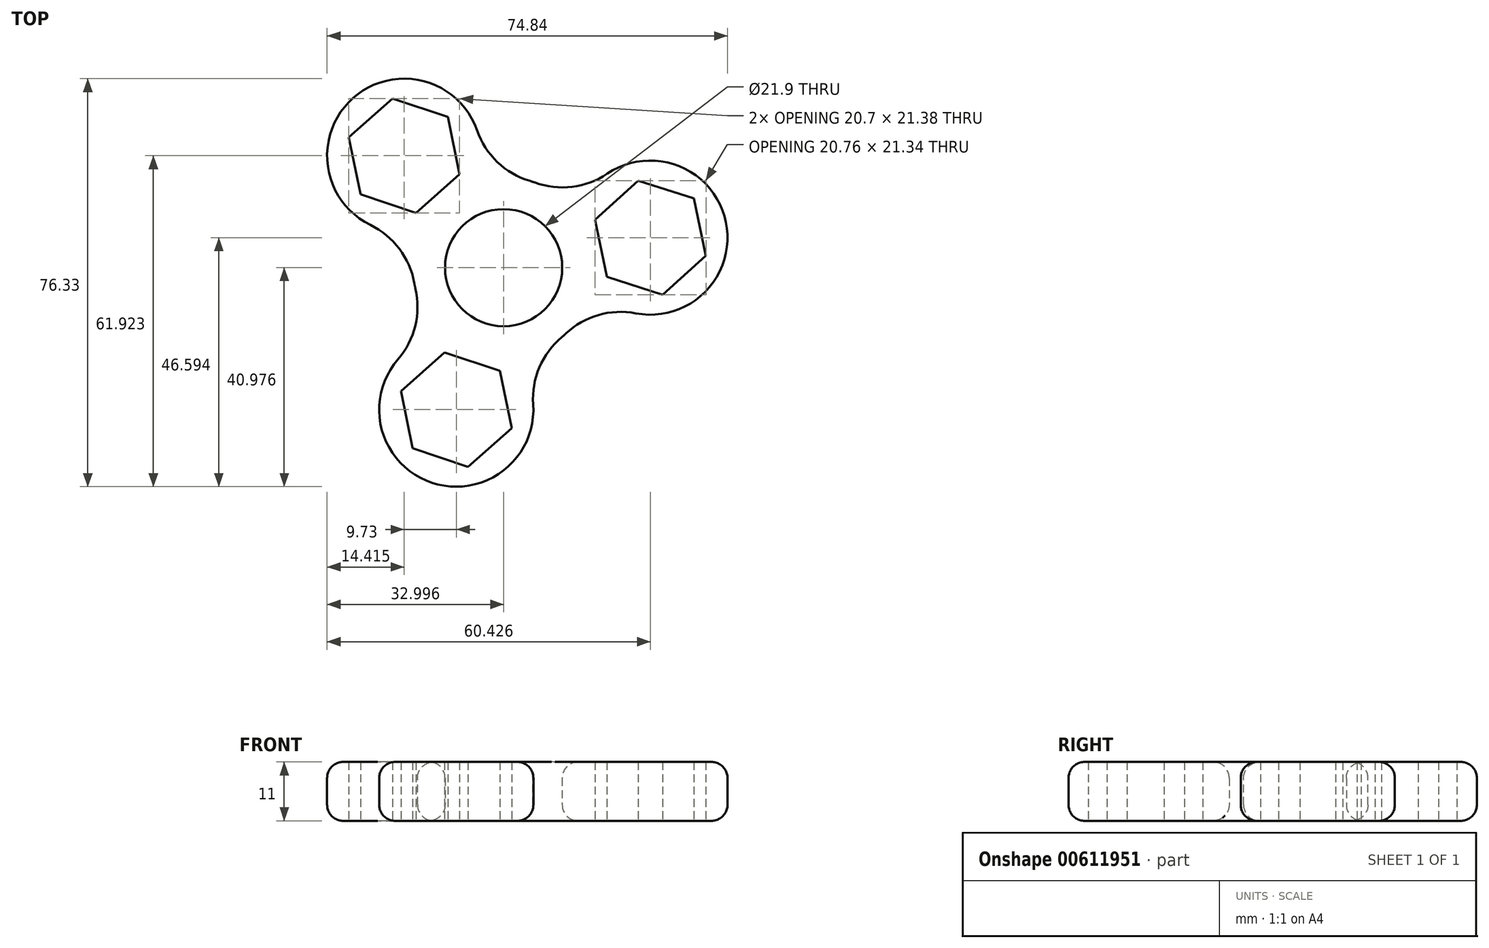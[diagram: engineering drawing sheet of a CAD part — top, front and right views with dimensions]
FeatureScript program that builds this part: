
annotation { "Feature Type Name" : "Feature", "Feature Type Description" : "" }
export const myFeature = defineFeature(function(context is Context, id is Id, definition is map)
    precondition{}
    {
        {
            var Q0;
            Q0=qCreatedBy(makeId("Top.planeOp"),FACE);
            var sketch = newSketch(context, id + "F0", { "sketchPlane" : qUnion([Q0])});
            skCircle(sketch, "E0", {"center": v(0.14, -0.37) * mm, "radius": 10.95 * mm});
            skCircle(sketch, "E1.0", {"center": v(0.14, -0.37) * mm, "radius": 16.95 * mm});
            skCircle(sketch, "E2.cCircle", {"center": v(0.14, -0.37) * mm, "radius": 14 * mm, "construction": true});
            skLineSegment(sketch, "E2.0", {"start": v(-18.44, 20.57) * mm, "end": v(27.57, 5.24) * mm, "construction": true});
            skLineSegment(sketch, "E2.1", {"start": v(27.57, 5.24) * mm, "end": v(-8.71, -26.94) * mm, "construction": true});
            skLineSegment(sketch, "E2.2", {"start": v(-8.71, -26.94) * mm, "end": v(-18.44, 20.57) * mm, "construction": true});
            skPoint(sketch, "E2.0.midPoint", {"position": v(4.56, 12.9) * mm});
            skCircle(sketch, "E3.cCircle", {"center": v(-18.44, 20.57) * mm, "radius": 9.45 * mm, "construction": true});
            skLineSegment(sketch, "E3.0", {"start": v(-28.8, 24.03) * mm, "end": v(-20.63, 31.26) * mm});
            skLineSegment(sketch, "E3.1", {"start": v(-20.63, 31.26) * mm, "end": v(-10.28, 27.8) * mm});
            skLineSegment(sketch, "E3.2", {"start": v(-10.28, 27.8) * mm, "end": v(-8.1, 17.12) * mm});
            skLineSegment(sketch, "E3.3", {"start": v(-8.1, 17.12) * mm, "end": v(-16.26, 9.88) * mm});
            skLineSegment(sketch, "E3.4", {"start": v(-16.26, 9.88) * mm, "end": v(-26.61, 13.34) * mm});
            skLineSegment(sketch, "E3.5", {"start": v(-26.61, 13.34) * mm, "end": v(-28.8, 24.03) * mm});
            skPoint(sketch, "E3.0.midPoint", {"position": v(-24.71, 27.65) * mm});
            skCircle(sketch, "E4.cCircle", {"center": v(27.57, 5.24) * mm, "radius": 9.45 * mm, "construction": true});
            skLineSegment(sketch, "E4.0", {"start": v(35.67, 12.55) * mm, "end": v(37.95, 1.88) * mm});
            skLineSegment(sketch, "E4.1", {"start": v(37.95, 1.88) * mm, "end": v(29.85, -5.43) * mm});
            skLineSegment(sketch, "E4.2", {"start": v(29.85, -5.43) * mm, "end": v(19.47, -2.07) * mm});
            skLineSegment(sketch, "E4.3", {"start": v(19.47, -2.07) * mm, "end": v(17.18, 8.6) * mm});
            skLineSegment(sketch, "E4.4", {"start": v(17.18, 8.6) * mm, "end": v(25.29, 15.91) * mm});
            skLineSegment(sketch, "E4.5", {"start": v(25.29, 15.91) * mm, "end": v(35.67, 12.55) * mm});
            skPoint(sketch, "E4.0.midPoint", {"position": v(36.8, 7.22) * mm});
            skCircle(sketch, "E5.cCircle", {"center": v(-8.71, -26.94) * mm, "radius": 9.45 * mm, "construction": true});
            skLineSegment(sketch, "E5.0", {"start": v(-6.53, -37.63) * mm, "end": v(-16.88, -34.17) * mm});
            skLineSegment(sketch, "E5.1", {"start": v(-16.88, -34.17) * mm, "end": v(-19.06, -23.48) * mm});
            skLineSegment(sketch, "E5.2", {"start": v(-19.06, -23.48) * mm, "end": v(-10.9, -16.25) * mm});
            skLineSegment(sketch, "E5.3", {"start": v(-10.9, -16.25) * mm, "end": v(-0.55, -19.7) * mm});
            skLineSegment(sketch, "E5.4", {"start": v(-0.55, -19.7) * mm, "end": v(1.63, -30.4) * mm});
            skLineSegment(sketch, "E5.5", {"start": v(1.63, -30.4) * mm, "end": v(-6.53, -37.63) * mm});
            skPoint(sketch, "E5.0.midPoint", {"position": v(-11.7, -35.9) * mm});
            skCircle(sketch, "E6", {"center": v(-8.71, -26.94) * mm, "radius": 14.41 * mm});
            skCircle(sketch, "E7", {"center": v(27.57, 5.24) * mm, "radius": 14.41 * mm});
            skCircle(sketch, "E8", {"center": v(-18.44, 20.57) * mm, "radius": 14.41 * mm});
            skPoint(sketch, "E9.endSnap0", {"position": v(-13.58, -3.18) * mm});
            skLineSegment(sketch, "E10", {"start": v(0.14, -0.37) * mm, "end": v(51.26, 10.11) * mm, "construction": true});
            skLineSegment(sketch, "E11", {"start": v(0.14, -0.37) * mm, "end": v(-32.46, 36.46) * mm, "construction": true});
            skLineSegment(sketch, "E12", {"start": v(0.14, -0.37) * mm, "end": v(-11.7, -35.9) * mm, "construction": true});
            skPoint(sketch, "E13.trimOffspring.end.orphan", {"position": v(-13.58, 9.59) * mm});
            skSolve(sketch);
        }
        {
            var Q0;
            Q0 = qSketchRegion(id + "F0", true);
            extrude(context, id + "F1", {"entities" : qUnion([Q0]), "depth" : 11 * mm, "offsetDistance" : 25 * mm});
        }
        {
            var Q0;
            {var subQ0=sQuery(id+"F0.wireOp",EDGE,"E7");var subQ1=sQuery(id+"F0.wireOp",EDGE,"E1.0");Q0=makeQuery(id+"F1.opExtrude","SWEPT_EDGE",EDGE,{"disambiguationData":[OSD([subQ1,subQ0]),TDD([makeQuery(id+"F0.imprint","INTERSECT",VERTEX,{"disambiguationData":[OD(1.0)],"derivedFrom":[subQ1,subQ0]})])]});}
            var Q1;
            {var subQ0=sQuery(id+"F0.wireOp",EDGE,"E6");var subQ1=sQuery(id+"F0.wireOp",EDGE,"E1.0");Q1=makeQuery(id+"F1.opExtrude","SWEPT_EDGE",EDGE,{"disambiguationData":[OSD([subQ1,subQ0]),TDD([makeQuery(id+"F0.imprint","INTERSECT",VERTEX,{"disambiguationData":[OD(1.0)],"derivedFrom":[subQ1,subQ0]})])]});}
            var Q2;
            {var subQ0=sQuery(id+"F0.wireOp",EDGE,"E6");var subQ1=sQuery(id+"F0.wireOp",EDGE,"E1.0");Q2=makeQuery(id+"F1.opExtrude","SWEPT_EDGE",EDGE,{"disambiguationData":[OSD([subQ1,subQ0]),TDD([makeQuery(id+"F0.imprint","INTERSECT",VERTEX,{"disambiguationData":[OD(0.0)],"derivedFrom":[subQ1,subQ0]})])]});}
            var Q3;
            {var subQ0=sQuery(id+"F0.wireOp",EDGE,"E8");var subQ1=sQuery(id+"F0.wireOp",EDGE,"E1.0");Q3=makeQuery(id+"F1.opExtrude","SWEPT_EDGE",EDGE,{"disambiguationData":[OSD([subQ1,subQ0]),TDD([makeQuery(id+"F0.imprint","INTERSECT",VERTEX,{"disambiguationData":[OD(1.0)],"derivedFrom":[subQ1,subQ0]})])]});}
            var Q4;
            {var subQ0=sQuery(id+"F0.wireOp",EDGE,"E8");var subQ1=sQuery(id+"F0.wireOp",EDGE,"E1.0");Q4=makeQuery(id+"F1.opExtrude","SWEPT_EDGE",EDGE,{"disambiguationData":[OSD([subQ1,subQ0]),TDD([makeQuery(id+"F0.imprint","INTERSECT",VERTEX,{"disambiguationData":[OD(0.0)],"derivedFrom":[subQ1,subQ0]})])]});}
            var Q5;
            {var subQ0=sQuery(id+"F0.wireOp",EDGE,"E7");var subQ1=sQuery(id+"F0.wireOp",EDGE,"E1.0");Q5=makeQuery(id+"F1.opExtrude","SWEPT_EDGE",EDGE,{"disambiguationData":[OSD([subQ1,subQ0]),TDD([makeQuery(id+"F0.imprint","INTERSECT",VERTEX,{"disambiguationData":[OD(0.0)],"derivedFrom":[subQ1,subQ0]})])]});}
            fillet(context, id + "F2", {"entities" : qUnion([Q0, Q1, Q2, Q3, Q4, Q5]), "radius" : 15 * mm, "tangentPropagation" : true, "allowEdgeOverflow" : false});
        }
        {
            var Q0;
            Q0=makeQuery(id+"F1.opExtrude","CAP_EDGE",EDGE,{"disambiguationData":[OSD([sQuery(id+"F0.wireOp",EDGE,"E8")])],"isStart":true});
            var Q1;
            Q1=makeQuery(id+"F1.opExtrude","CAP_EDGE",EDGE,{"disambiguationData":[OSD([sQuery(id+"F0.wireOp",EDGE,"E7")])],"isStart":true});
            var Q2;
            {var subQ0=sQuery(id+"F0.wireOp",EDGE,"E6");var subQ1=sQuery(id+"F0.wireOp",EDGE,"E1.0");Q2=makeQuery(id+"F2.opFillet","BLEND_EDGE",EDGE,{"blendedFrom":[makeQuery(id+"F1.opExtrude","SWEPT_EDGE",EDGE,{"disambiguationData":[OSD([subQ1,subQ0]),TDD([makeQuery(id+"F0.imprint","INTERSECT",VERTEX,{"disambiguationData":[OD(1.0)],"derivedFrom":[subQ1,subQ0]})])]}),makeQuery(id+"F1.opExtrude","CAP_FACE",FACE,{"disambiguationData":[OSD([sQuery(id+"F0.wireOp",EDGE,"E0"),subQ1,sQuery(id+"F0.wireOp",EDGE,"E3.0"),sQuery(id+"F0.wireOp",EDGE,"E3.1"),sQuery(id+"F0.wireOp",EDGE,"E3.2"),sQuery(id+"F0.wireOp",EDGE,"E3.3"),sQuery(id+"F0.wireOp",EDGE,"E3.4"),sQuery(id+"F0.wireOp",EDGE,"E3.5"),sQuery(id+"F0.wireOp",EDGE,"E4.0"),sQuery(id+"F0.wireOp",EDGE,"E4.1"),sQuery(id+"F0.wireOp",EDGE,"E4.2"),sQuery(id+"F0.wireOp",EDGE,"E4.3"),sQuery(id+"F0.wireOp",EDGE,"E4.4"),sQuery(id+"F0.wireOp",EDGE,"E4.5"),sQuery(id+"F0.wireOp",EDGE,"E5.0"),sQuery(id+"F0.wireOp",EDGE,"E5.1"),sQuery(id+"F0.wireOp",EDGE,"E5.2"),sQuery(id+"F0.wireOp",EDGE,"E5.3"),sQuery(id+"F0.wireOp",EDGE,"E5.4"),sQuery(id+"F0.wireOp",EDGE,"E5.5"),subQ0,sQuery(id+"F0.wireOp",EDGE,"E7"),sQuery(id+"F0.wireOp",EDGE,"E8")])],"isStart":true})],"blendedInto":[makeQuery(id+"F1.opExtrude","CAP_FACE",FACE,{"disambiguationData":[OSD([sQuery(id+"F0.wireOp",EDGE,"E0"),subQ1,sQuery(id+"F0.wireOp",EDGE,"E3.0"),sQuery(id+"F0.wireOp",EDGE,"E3.1"),sQuery(id+"F0.wireOp",EDGE,"E3.2"),sQuery(id+"F0.wireOp",EDGE,"E3.3"),sQuery(id+"F0.wireOp",EDGE,"E3.4"),sQuery(id+"F0.wireOp",EDGE,"E3.5"),sQuery(id+"F0.wireOp",EDGE,"E4.0"),sQuery(id+"F0.wireOp",EDGE,"E4.1"),sQuery(id+"F0.wireOp",EDGE,"E4.2"),sQuery(id+"F0.wireOp",EDGE,"E4.3"),sQuery(id+"F0.wireOp",EDGE,"E4.4"),sQuery(id+"F0.wireOp",EDGE,"E4.5"),sQuery(id+"F0.wireOp",EDGE,"E5.0"),sQuery(id+"F0.wireOp",EDGE,"E5.1"),sQuery(id+"F0.wireOp",EDGE,"E5.2"),sQuery(id+"F0.wireOp",EDGE,"E5.3"),sQuery(id+"F0.wireOp",EDGE,"E5.4"),sQuery(id+"F0.wireOp",EDGE,"E5.5"),subQ0,sQuery(id+"F0.wireOp",EDGE,"E7"),sQuery(id+"F0.wireOp",EDGE,"E8")])],"isStart":true})]});}
            fillet(context, id + "F3", {"entities" : qUnion([Q0, Q1, Q2]), "radius" : 3 * mm, "tangentPropagation" : true, "allowEdgeOverflow" : false});
        }
        {
            var Q0;
            {var subQ0=sQuery(id+"F0.wireOp",EDGE,"E6");var subQ1=sQuery(id+"F0.wireOp",EDGE,"E1.0");Q0=makeQuery(id+"F2.opFillet","BLEND_EDGE",EDGE,{"blendedFrom":[makeQuery(id+"F1.opExtrude","SWEPT_EDGE",EDGE,{"disambiguationData":[OSD([subQ1,subQ0]),TDD([makeQuery(id+"F0.imprint","INTERSECT",VERTEX,{"disambiguationData":[OD(0.0)],"derivedFrom":[subQ1,subQ0]})])]}),makeQuery(id+"F1.opExtrude","CAP_FACE",FACE,{"disambiguationData":[OSD([sQuery(id+"F0.wireOp",EDGE,"E0"),subQ1,sQuery(id+"F0.wireOp",EDGE,"E3.0"),sQuery(id+"F0.wireOp",EDGE,"E3.1"),sQuery(id+"F0.wireOp",EDGE,"E3.2"),sQuery(id+"F0.wireOp",EDGE,"E3.3"),sQuery(id+"F0.wireOp",EDGE,"E3.4"),sQuery(id+"F0.wireOp",EDGE,"E3.5"),sQuery(id+"F0.wireOp",EDGE,"E4.0"),sQuery(id+"F0.wireOp",EDGE,"E4.1"),sQuery(id+"F0.wireOp",EDGE,"E4.2"),sQuery(id+"F0.wireOp",EDGE,"E4.3"),sQuery(id+"F0.wireOp",EDGE,"E4.4"),sQuery(id+"F0.wireOp",EDGE,"E4.5"),sQuery(id+"F0.wireOp",EDGE,"E5.0"),sQuery(id+"F0.wireOp",EDGE,"E5.1"),sQuery(id+"F0.wireOp",EDGE,"E5.2"),sQuery(id+"F0.wireOp",EDGE,"E5.3"),sQuery(id+"F0.wireOp",EDGE,"E5.4"),sQuery(id+"F0.wireOp",EDGE,"E5.5"),subQ0,sQuery(id+"F0.wireOp",EDGE,"E7"),sQuery(id+"F0.wireOp",EDGE,"E8")])],"isStart":false})],"blendedInto":[makeQuery(id+"F1.opExtrude","CAP_FACE",FACE,{"disambiguationData":[OSD([sQuery(id+"F0.wireOp",EDGE,"E0"),subQ1,sQuery(id+"F0.wireOp",EDGE,"E3.0"),sQuery(id+"F0.wireOp",EDGE,"E3.1"),sQuery(id+"F0.wireOp",EDGE,"E3.2"),sQuery(id+"F0.wireOp",EDGE,"E3.3"),sQuery(id+"F0.wireOp",EDGE,"E3.4"),sQuery(id+"F0.wireOp",EDGE,"E3.5"),sQuery(id+"F0.wireOp",EDGE,"E4.0"),sQuery(id+"F0.wireOp",EDGE,"E4.1"),sQuery(id+"F0.wireOp",EDGE,"E4.2"),sQuery(id+"F0.wireOp",EDGE,"E4.3"),sQuery(id+"F0.wireOp",EDGE,"E4.4"),sQuery(id+"F0.wireOp",EDGE,"E4.5"),sQuery(id+"F0.wireOp",EDGE,"E5.0"),sQuery(id+"F0.wireOp",EDGE,"E5.1"),sQuery(id+"F0.wireOp",EDGE,"E5.2"),sQuery(id+"F0.wireOp",EDGE,"E5.3"),sQuery(id+"F0.wireOp",EDGE,"E5.4"),sQuery(id+"F0.wireOp",EDGE,"E5.5"),subQ0,sQuery(id+"F0.wireOp",EDGE,"E7"),sQuery(id+"F0.wireOp",EDGE,"E8")])],"isStart":false})]});}
            var Q1;
            Q1=makeQuery(id+"F1.opExtrude","CAP_EDGE",EDGE,{"disambiguationData":[OSD([sQuery(id+"F0.wireOp",EDGE,"E6")])],"isStart":false});
            var Q2;
            {var subQ0=sQuery(id+"F0.wireOp",EDGE,"E6");var subQ1=sQuery(id+"F0.wireOp",EDGE,"E1.0");Q2=makeQuery(id+"F2.opFillet","BLEND_EDGE",EDGE,{"blendedFrom":[makeQuery(id+"F1.opExtrude","SWEPT_EDGE",EDGE,{"disambiguationData":[OSD([subQ1,subQ0]),TDD([makeQuery(id+"F0.imprint","INTERSECT",VERTEX,{"disambiguationData":[OD(1.0)],"derivedFrom":[subQ1,subQ0]})])]}),makeQuery(id+"F1.opExtrude","CAP_FACE",FACE,{"disambiguationData":[OSD([sQuery(id+"F0.wireOp",EDGE,"E0"),subQ1,sQuery(id+"F0.wireOp",EDGE,"E3.0"),sQuery(id+"F0.wireOp",EDGE,"E3.1"),sQuery(id+"F0.wireOp",EDGE,"E3.2"),sQuery(id+"F0.wireOp",EDGE,"E3.3"),sQuery(id+"F0.wireOp",EDGE,"E3.4"),sQuery(id+"F0.wireOp",EDGE,"E3.5"),sQuery(id+"F0.wireOp",EDGE,"E4.0"),sQuery(id+"F0.wireOp",EDGE,"E4.1"),sQuery(id+"F0.wireOp",EDGE,"E4.2"),sQuery(id+"F0.wireOp",EDGE,"E4.3"),sQuery(id+"F0.wireOp",EDGE,"E4.4"),sQuery(id+"F0.wireOp",EDGE,"E4.5"),sQuery(id+"F0.wireOp",EDGE,"E5.0"),sQuery(id+"F0.wireOp",EDGE,"E5.1"),sQuery(id+"F0.wireOp",EDGE,"E5.2"),sQuery(id+"F0.wireOp",EDGE,"E5.3"),sQuery(id+"F0.wireOp",EDGE,"E5.4"),sQuery(id+"F0.wireOp",EDGE,"E5.5"),subQ0,sQuery(id+"F0.wireOp",EDGE,"E7"),sQuery(id+"F0.wireOp",EDGE,"E8")])],"isStart":false})],"blendedInto":[makeQuery(id+"F1.opExtrude","CAP_FACE",FACE,{"disambiguationData":[OSD([sQuery(id+"F0.wireOp",EDGE,"E0"),subQ1,sQuery(id+"F0.wireOp",EDGE,"E3.0"),sQuery(id+"F0.wireOp",EDGE,"E3.1"),sQuery(id+"F0.wireOp",EDGE,"E3.2"),sQuery(id+"F0.wireOp",EDGE,"E3.3"),sQuery(id+"F0.wireOp",EDGE,"E3.4"),sQuery(id+"F0.wireOp",EDGE,"E3.5"),sQuery(id+"F0.wireOp",EDGE,"E4.0"),sQuery(id+"F0.wireOp",EDGE,"E4.1"),sQuery(id+"F0.wireOp",EDGE,"E4.2"),sQuery(id+"F0.wireOp",EDGE,"E4.3"),sQuery(id+"F0.wireOp",EDGE,"E4.4"),sQuery(id+"F0.wireOp",EDGE,"E4.5"),sQuery(id+"F0.wireOp",EDGE,"E5.0"),sQuery(id+"F0.wireOp",EDGE,"E5.1"),sQuery(id+"F0.wireOp",EDGE,"E5.2"),sQuery(id+"F0.wireOp",EDGE,"E5.3"),sQuery(id+"F0.wireOp",EDGE,"E5.4"),sQuery(id+"F0.wireOp",EDGE,"E5.5"),subQ0,sQuery(id+"F0.wireOp",EDGE,"E7"),sQuery(id+"F0.wireOp",EDGE,"E8")])],"isStart":false})]});}
            var Q3;
            {var subQ0=sQuery(id+"F0.wireOp",EDGE,"E7");var subQ1=sQuery(id+"F0.wireOp",EDGE,"E1.0");Q3=makeQuery(id+"F2.opFillet","BLEND_EDGE",EDGE,{"blendedFrom":[makeQuery(id+"F1.opExtrude","SWEPT_EDGE",EDGE,{"disambiguationData":[OSD([subQ1,subQ0]),TDD([makeQuery(id+"F0.imprint","INTERSECT",VERTEX,{"disambiguationData":[OD(1.0)],"derivedFrom":[subQ1,subQ0]})])]}),makeQuery(id+"F1.opExtrude","CAP_FACE",FACE,{"disambiguationData":[OSD([sQuery(id+"F0.wireOp",EDGE,"E0"),subQ1,sQuery(id+"F0.wireOp",EDGE,"E3.0"),sQuery(id+"F0.wireOp",EDGE,"E3.1"),sQuery(id+"F0.wireOp",EDGE,"E3.2"),sQuery(id+"F0.wireOp",EDGE,"E3.3"),sQuery(id+"F0.wireOp",EDGE,"E3.4"),sQuery(id+"F0.wireOp",EDGE,"E3.5"),sQuery(id+"F0.wireOp",EDGE,"E4.0"),sQuery(id+"F0.wireOp",EDGE,"E4.1"),sQuery(id+"F0.wireOp",EDGE,"E4.2"),sQuery(id+"F0.wireOp",EDGE,"E4.3"),sQuery(id+"F0.wireOp",EDGE,"E4.4"),sQuery(id+"F0.wireOp",EDGE,"E4.5"),sQuery(id+"F0.wireOp",EDGE,"E5.0"),sQuery(id+"F0.wireOp",EDGE,"E5.1"),sQuery(id+"F0.wireOp",EDGE,"E5.2"),sQuery(id+"F0.wireOp",EDGE,"E5.3"),sQuery(id+"F0.wireOp",EDGE,"E5.4"),sQuery(id+"F0.wireOp",EDGE,"E5.5"),sQuery(id+"F0.wireOp",EDGE,"E6"),subQ0,sQuery(id+"F0.wireOp",EDGE,"E8")])],"isStart":false})],"blendedInto":[makeQuery(id+"F1.opExtrude","CAP_FACE",FACE,{"disambiguationData":[OSD([sQuery(id+"F0.wireOp",EDGE,"E0"),subQ1,sQuery(id+"F0.wireOp",EDGE,"E3.0"),sQuery(id+"F0.wireOp",EDGE,"E3.1"),sQuery(id+"F0.wireOp",EDGE,"E3.2"),sQuery(id+"F0.wireOp",EDGE,"E3.3"),sQuery(id+"F0.wireOp",EDGE,"E3.4"),sQuery(id+"F0.wireOp",EDGE,"E3.5"),sQuery(id+"F0.wireOp",EDGE,"E4.0"),sQuery(id+"F0.wireOp",EDGE,"E4.1"),sQuery(id+"F0.wireOp",EDGE,"E4.2"),sQuery(id+"F0.wireOp",EDGE,"E4.3"),sQuery(id+"F0.wireOp",EDGE,"E4.4"),sQuery(id+"F0.wireOp",EDGE,"E4.5"),sQuery(id+"F0.wireOp",EDGE,"E5.0"),sQuery(id+"F0.wireOp",EDGE,"E5.1"),sQuery(id+"F0.wireOp",EDGE,"E5.2"),sQuery(id+"F0.wireOp",EDGE,"E5.3"),sQuery(id+"F0.wireOp",EDGE,"E5.4"),sQuery(id+"F0.wireOp",EDGE,"E5.5"),sQuery(id+"F0.wireOp",EDGE,"E6"),subQ0,sQuery(id+"F0.wireOp",EDGE,"E8")])],"isStart":false})]});}
            var Q4;
            Q4=makeQuery(id+"F1.opExtrude","CAP_EDGE",EDGE,{"disambiguationData":[OSD([sQuery(id+"F0.wireOp",EDGE,"E7")])],"isStart":false});
            var Q5;
            {var subQ0=sQuery(id+"F0.wireOp",EDGE,"E7");var subQ1=sQuery(id+"F0.wireOp",EDGE,"E1.0");Q5=makeQuery(id+"F2.opFillet","BLEND_EDGE",EDGE,{"blendedFrom":[makeQuery(id+"F1.opExtrude","SWEPT_EDGE",EDGE,{"disambiguationData":[OSD([subQ1,subQ0]),TDD([makeQuery(id+"F0.imprint","INTERSECT",VERTEX,{"disambiguationData":[OD(0.0)],"derivedFrom":[subQ1,subQ0]})])]}),makeQuery(id+"F1.opExtrude","CAP_FACE",FACE,{"disambiguationData":[OSD([sQuery(id+"F0.wireOp",EDGE,"E0"),subQ1,sQuery(id+"F0.wireOp",EDGE,"E3.0"),sQuery(id+"F0.wireOp",EDGE,"E3.1"),sQuery(id+"F0.wireOp",EDGE,"E3.2"),sQuery(id+"F0.wireOp",EDGE,"E3.3"),sQuery(id+"F0.wireOp",EDGE,"E3.4"),sQuery(id+"F0.wireOp",EDGE,"E3.5"),sQuery(id+"F0.wireOp",EDGE,"E4.0"),sQuery(id+"F0.wireOp",EDGE,"E4.1"),sQuery(id+"F0.wireOp",EDGE,"E4.2"),sQuery(id+"F0.wireOp",EDGE,"E4.3"),sQuery(id+"F0.wireOp",EDGE,"E4.4"),sQuery(id+"F0.wireOp",EDGE,"E4.5"),sQuery(id+"F0.wireOp",EDGE,"E5.0"),sQuery(id+"F0.wireOp",EDGE,"E5.1"),sQuery(id+"F0.wireOp",EDGE,"E5.2"),sQuery(id+"F0.wireOp",EDGE,"E5.3"),sQuery(id+"F0.wireOp",EDGE,"E5.4"),sQuery(id+"F0.wireOp",EDGE,"E5.5"),sQuery(id+"F0.wireOp",EDGE,"E6"),subQ0,sQuery(id+"F0.wireOp",EDGE,"E8")])],"isStart":false})],"blendedInto":[makeQuery(id+"F1.opExtrude","CAP_FACE",FACE,{"disambiguationData":[OSD([sQuery(id+"F0.wireOp",EDGE,"E0"),subQ1,sQuery(id+"F0.wireOp",EDGE,"E3.0"),sQuery(id+"F0.wireOp",EDGE,"E3.1"),sQuery(id+"F0.wireOp",EDGE,"E3.2"),sQuery(id+"F0.wireOp",EDGE,"E3.3"),sQuery(id+"F0.wireOp",EDGE,"E3.4"),sQuery(id+"F0.wireOp",EDGE,"E3.5"),sQuery(id+"F0.wireOp",EDGE,"E4.0"),sQuery(id+"F0.wireOp",EDGE,"E4.1"),sQuery(id+"F0.wireOp",EDGE,"E4.2"),sQuery(id+"F0.wireOp",EDGE,"E4.3"),sQuery(id+"F0.wireOp",EDGE,"E4.4"),sQuery(id+"F0.wireOp",EDGE,"E4.5"),sQuery(id+"F0.wireOp",EDGE,"E5.0"),sQuery(id+"F0.wireOp",EDGE,"E5.1"),sQuery(id+"F0.wireOp",EDGE,"E5.2"),sQuery(id+"F0.wireOp",EDGE,"E5.3"),sQuery(id+"F0.wireOp",EDGE,"E5.4"),sQuery(id+"F0.wireOp",EDGE,"E5.5"),sQuery(id+"F0.wireOp",EDGE,"E6"),subQ0,sQuery(id+"F0.wireOp",EDGE,"E8")])],"isStart":false})]});}
            var Q6;
            {var subQ0=sQuery(id+"F0.wireOp",EDGE,"E8");var subQ1=sQuery(id+"F0.wireOp",EDGE,"E1.0");Q6=makeQuery(id+"F2.opFillet","BLEND_EDGE",EDGE,{"blendedFrom":[makeQuery(id+"F1.opExtrude","SWEPT_EDGE",EDGE,{"disambiguationData":[OSD([subQ1,subQ0]),TDD([makeQuery(id+"F0.imprint","INTERSECT",VERTEX,{"disambiguationData":[OD(0.0)],"derivedFrom":[subQ1,subQ0]})])]}),makeQuery(id+"F1.opExtrude","CAP_FACE",FACE,{"disambiguationData":[OSD([sQuery(id+"F0.wireOp",EDGE,"E0"),subQ1,sQuery(id+"F0.wireOp",EDGE,"E3.0"),sQuery(id+"F0.wireOp",EDGE,"E3.1"),sQuery(id+"F0.wireOp",EDGE,"E3.2"),sQuery(id+"F0.wireOp",EDGE,"E3.3"),sQuery(id+"F0.wireOp",EDGE,"E3.4"),sQuery(id+"F0.wireOp",EDGE,"E3.5"),sQuery(id+"F0.wireOp",EDGE,"E4.0"),sQuery(id+"F0.wireOp",EDGE,"E4.1"),sQuery(id+"F0.wireOp",EDGE,"E4.2"),sQuery(id+"F0.wireOp",EDGE,"E4.3"),sQuery(id+"F0.wireOp",EDGE,"E4.4"),sQuery(id+"F0.wireOp",EDGE,"E4.5"),sQuery(id+"F0.wireOp",EDGE,"E5.0"),sQuery(id+"F0.wireOp",EDGE,"E5.1"),sQuery(id+"F0.wireOp",EDGE,"E5.2"),sQuery(id+"F0.wireOp",EDGE,"E5.3"),sQuery(id+"F0.wireOp",EDGE,"E5.4"),sQuery(id+"F0.wireOp",EDGE,"E5.5"),sQuery(id+"F0.wireOp",EDGE,"E6"),sQuery(id+"F0.wireOp",EDGE,"E7"),subQ0])],"isStart":false})],"blendedInto":[makeQuery(id+"F1.opExtrude","CAP_FACE",FACE,{"disambiguationData":[OSD([sQuery(id+"F0.wireOp",EDGE,"E0"),subQ1,sQuery(id+"F0.wireOp",EDGE,"E3.0"),sQuery(id+"F0.wireOp",EDGE,"E3.1"),sQuery(id+"F0.wireOp",EDGE,"E3.2"),sQuery(id+"F0.wireOp",EDGE,"E3.3"),sQuery(id+"F0.wireOp",EDGE,"E3.4"),sQuery(id+"F0.wireOp",EDGE,"E3.5"),sQuery(id+"F0.wireOp",EDGE,"E4.0"),sQuery(id+"F0.wireOp",EDGE,"E4.1"),sQuery(id+"F0.wireOp",EDGE,"E4.2"),sQuery(id+"F0.wireOp",EDGE,"E4.3"),sQuery(id+"F0.wireOp",EDGE,"E4.4"),sQuery(id+"F0.wireOp",EDGE,"E4.5"),sQuery(id+"F0.wireOp",EDGE,"E5.0"),sQuery(id+"F0.wireOp",EDGE,"E5.1"),sQuery(id+"F0.wireOp",EDGE,"E5.2"),sQuery(id+"F0.wireOp",EDGE,"E5.3"),sQuery(id+"F0.wireOp",EDGE,"E5.4"),sQuery(id+"F0.wireOp",EDGE,"E5.5"),sQuery(id+"F0.wireOp",EDGE,"E6"),sQuery(id+"F0.wireOp",EDGE,"E7"),subQ0])],"isStart":false})]});}
            fillet(context, id + "F4", {"entities" : qUnion([Q0, Q1, Q2, Q3, Q4, Q5, Q6]), "radius" : 3 * mm, "tangentPropagation" : true, "allowEdgeOverflow" : false});
        }
        {
            var Q0;
            Q0=makeQuery(id+"F1.opExtrude","CAP_EDGE",EDGE,{"disambiguationData":[OSD([sQuery(id+"F0.wireOp",EDGE,"E0")])],"isStart":false});
            var Q1;
            Q1=makeQuery(id+"F1.opExtrude","CAP_EDGE",EDGE,{"disambiguationData":[OSD([sQuery(id+"F0.wireOp",EDGE,"E0")])],"isStart":true});
            fillet(context, id + "F5", {"entities" : qUnion([Q0, Q1]), "radius" : 3 * mm, "tangentPropagation" : true, "allowEdgeOverflow" : false});
        }
    });
